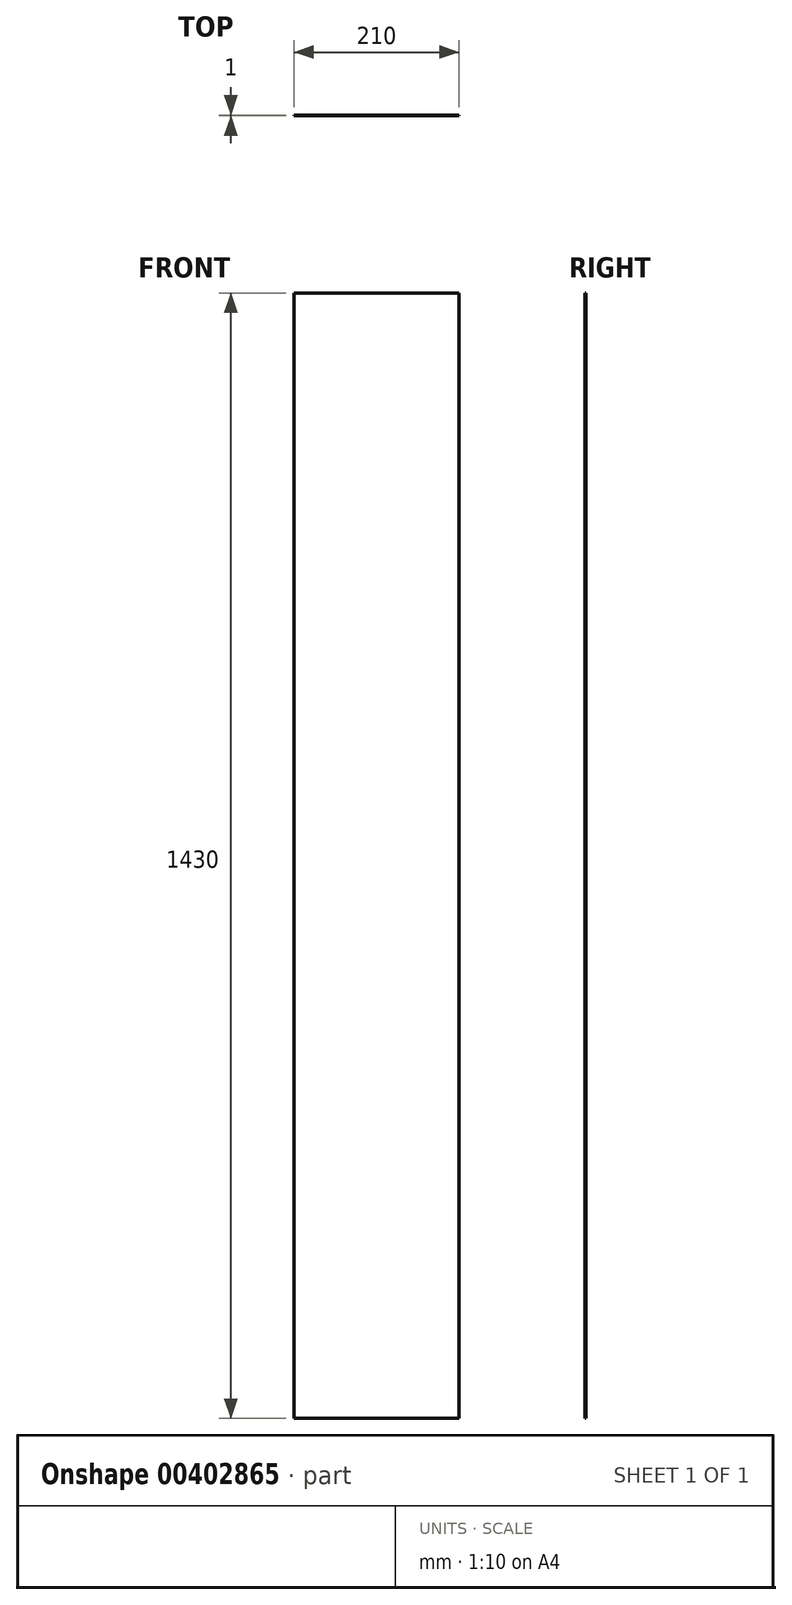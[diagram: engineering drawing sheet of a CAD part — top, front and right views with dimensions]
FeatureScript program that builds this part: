
annotation { "Feature Type Name" : "Feature", "Feature Type Description" : "" }
export const myFeature = defineFeature(function(context is Context, id is Id, definition is map)
    precondition{}
    {
        {
            var Q0;
            Q0=qCreatedBy(makeId("Front.planeOp"),FACE);
            var sketch = newSketch(context, id + "F0", { "sketchPlane" : qUnion([Q0])});
            skLineSegment(sketch, "E0.bottom", {"start": v(-105, 715) * mm, "end": v(105, 715) * mm});
            skLineSegment(sketch, "E0.top", {"start": v(-105, -715) * mm, "end": v(105, -715) * mm});
            skLineSegment(sketch, "E0.left", {"start": v(-105, 715) * mm, "end": v(-105, -715) * mm});
            skLineSegment(sketch, "E0.right", {"start": v(105, 715) * mm, "end": v(105, -715) * mm});
            skPoint(sketch, "E0.middle", {"position": v(0, 0) * mm});
            skSolve(sketch);
        }
        {
            var Q0;
            Q0=makeQuery(id+"F0.imprint","IMPRINT",FACE,{"disambiguationData":[TD([[makeQuery(id+"F0.imprint","IMPRINT",EDGE,{"derivedFrom":sQuery(id+"F0.wireOp",EDGE,"E0.bottom")}),-1.0]])]});
            extrude(context, id + "F1", {"entities" : qUnion([Q0]), "depth" : 1 * mm});
        }
    });
